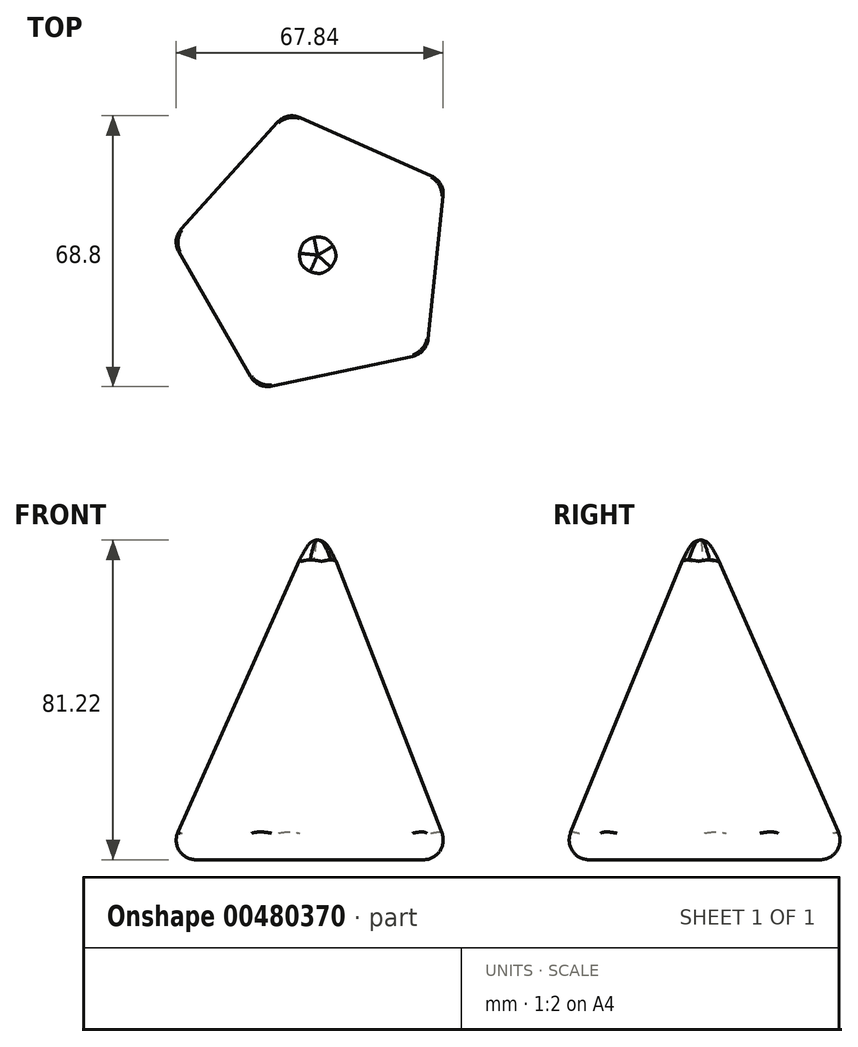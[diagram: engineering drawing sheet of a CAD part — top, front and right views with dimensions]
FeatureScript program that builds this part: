
annotation { "Feature Type Name" : "Feature", "Feature Type Description" : "" }
export const myFeature = defineFeature(function(context is Context, id is Id, definition is map)
    precondition{}
    {
        {
            var Q0;
            Q0=qCreatedBy(makeId("Top.planeOp"),FACE);
            var sketch = newSketch(context, id + "F0", { "sketchPlane" : qUnion([Q0])});
            skCircle(sketch, "E0.cCircle", {"center": v(0, 0) * mm, "radius": 39.9 * mm, "construction": true});
            skLineSegment(sketch, "E0.0", {"start": v(34.57, 19.94) * mm, "end": v(29.65, -26.72) * mm});
            skLineSegment(sketch, "E0.1", {"start": v(29.65, -26.72) * mm, "end": v(-16.25, -36.45) * mm});
            skLineSegment(sketch, "E0.2", {"start": v(-16.25, -36.45) * mm, "end": v(-39.69, 4.19) * mm});
            skLineSegment(sketch, "E0.3", {"start": v(-39.69, 4.19) * mm, "end": v(-8.28, 39.04) * mm});
            skLineSegment(sketch, "E0.4", {"start": v(-8.28, 39.04) * mm, "end": v(34.57, 19.94) * mm});
            skSolve(sketch);
        }
        {
            var Q0;
            Q0 = qSketchRegion(id + "F0", true);
            extrude(context, id + "F1", {"entities" : qUnion([Q0]), "depth" : 105.5 * mm, "hasDraft" : true, "draftAngle" : 20 * degree, "draftPullDirection" : true});
        }
        {
            var Q0;
            Q0=makeQuery(id+"F1.opExtrude","SWEPT_EDGE",EDGE,{"disambiguationData":[OSD([sQuery(id+"F0.wireOp",EDGE,"E0.1"),sQuery(id+"F0.wireOp",EDGE,"E0.2")])]});
            var Q1;
            Q1=makeQuery(id+"F1.opExtrude","SWEPT_EDGE",EDGE,{"disambiguationData":[OSD([sQuery(id+"F0.wireOp",EDGE,"E0.2"),sQuery(id+"F0.wireOp",EDGE,"E0.3")])]});
            var Q2;
            Q2=makeQuery(id+"F1.opExtrude","SWEPT_EDGE",EDGE,{"disambiguationData":[OSD([sQuery(id+"F0.wireOp",EDGE,"E0.0"),sQuery(id+"F0.wireOp",EDGE,"E0.1")])]});
            var Q3;
            Q3=makeQuery(id+"F1.opExtrude","CAP_EDGE",EDGE,{"disambiguationData":[OSD([sQuery(id+"F0.wireOp",EDGE,"E0.4")])],"isStart":true});
            var Q4;
            Q4=makeQuery(id+"F1.opExtrude","SWEPT_EDGE",EDGE,{"disambiguationData":[OSD([sQuery(id+"F0.wireOp",EDGE,"E0.3"),sQuery(id+"F0.wireOp",EDGE,"E0.4")])]});
            var Q5;
            Q5=makeQuery(id+"F1.opExtrude","CAP_EDGE",EDGE,{"disambiguationData":[OSD([sQuery(id+"F0.wireOp",EDGE,"E0.3")])],"isStart":true});
            var Q6;
            Q6=makeQuery(id+"F1.opExtrude","SWEPT_EDGE",EDGE,{"disambiguationData":[OSD([sQuery(id+"F0.wireOp",EDGE,"E0.0"),sQuery(id+"F0.wireOp",EDGE,"E0.4")])]});
            var Q7;
            Q7=makeQuery(id+"F1.opExtrude","CAP_EDGE",EDGE,{"disambiguationData":[OSD([sQuery(id+"F0.wireOp",EDGE,"E0.0")])],"isStart":true});
            var Q8;
            Q8=makeQuery(id+"F1.opExtrude","CAP_EDGE",EDGE,{"disambiguationData":[OSD([sQuery(id+"F0.wireOp",EDGE,"E0.1")])],"isStart":true});
            var Q9;
            Q9=makeQuery(id+"F1.opExtrude","CAP_EDGE",EDGE,{"disambiguationData":[OSD([sQuery(id+"F0.wireOp",EDGE,"E0.2")])],"isStart":true});
            fillet(context, id + "F2", {"entities" : qUnion([Q0, Q1, Q2, Q3, Q4, Q5, Q6, Q7, Q8, Q9]), "radius" : 5 * mm, "tangentPropagation" : true, "allowEdgeOverflow" : false});
        }
    });
